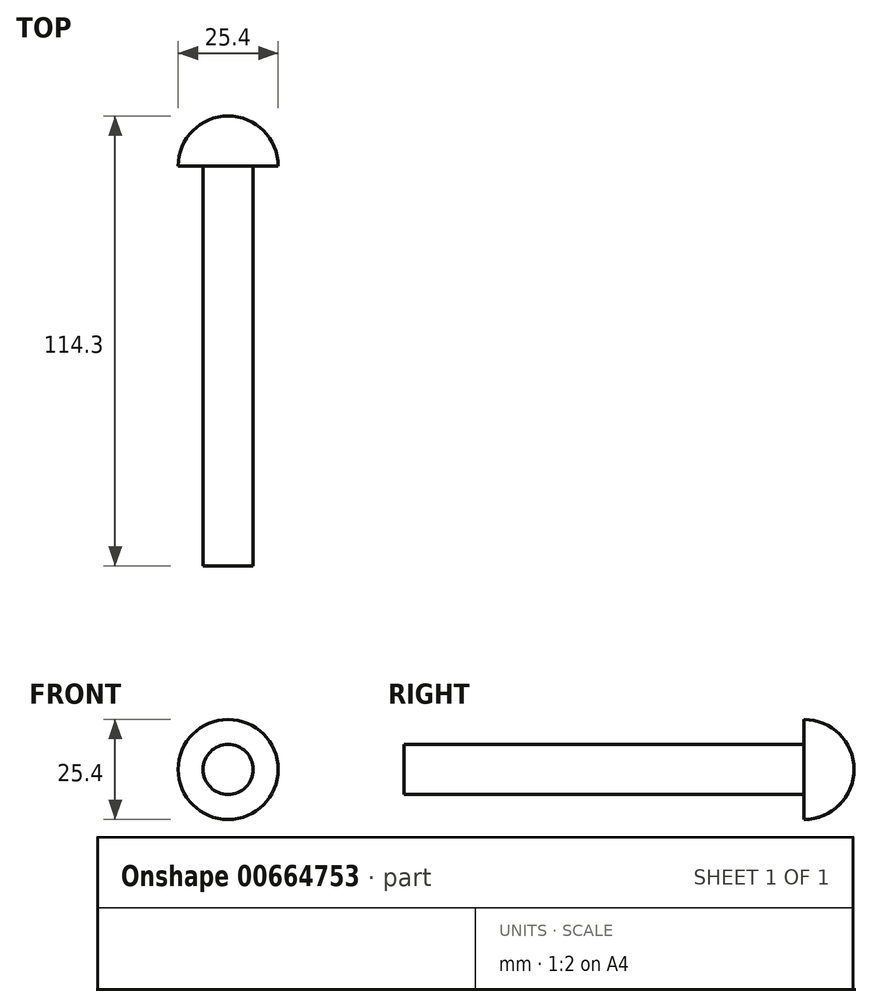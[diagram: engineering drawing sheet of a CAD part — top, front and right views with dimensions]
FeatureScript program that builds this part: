
annotation { "Feature Type Name" : "Feature", "Feature Type Description" : "" }
export const myFeature = defineFeature(function(context is Context, id is Id, definition is map)
    precondition{}
    {
        {
            var Q0;
            Q0=qCreatedBy(makeId("Front.planeOp"),FACE);
            var sketch = newSketch(context, id + "F0", { "sketchPlane" : qUnion([Q0])});
            skCircle(sketch, "E0", {"center": v(0, 0) * mm, "radius": 6.35 * mm});
            skSolve(sketch);
        }
        {
            var Q0;
            Q0 = qSketchRegion(id + "F0", true);
            extrude(context, id + "F1", {"entities" : qUnion([Q0]), "depth" : 101.6 * mm, "offsetDistance" : 25.4 * mm});
        }
        {
            var Q0;
            Q0=qCreatedBy(makeId("Right.planeOp"),FACE);
            var sketch = newSketch(context, id + "F2", { "sketchPlane" : qUnion([Q0])});
            skLineSegment(sketch, "E1", {"start": v(12.7, 0) * mm, "end": v(0, 0) * mm});
            skLineSegment(sketch, "E2", {"start": v(0, 0) * mm, "end": v(0, 12.7) * mm});
            skLineSegment(sketch, "E3", {"start": v(0, 12.7) * mm, "end": v(0, -12.43) * mm});
            skArc(sketch, "E4", {"start": v(0, 12.7) * mm, "mid": v(8.98, 8.98) * mm, "end": v(12.7, 0) * mm});
            skSolve(sketch);
        }
        {
            var Q0;
            Q0 = qSketchRegion(id + "F2", true);
            var Q1;
            Q1=sQuery(id+"F2.wireOp",EDGE,"E1");
            revolve(context, id + "F3", {"operationType" : NewBodyOperationType.ADD, "surfaceOperationType" : NewSurfaceOperationType.NEW, "entities" : qUnion([Q0]), "axis" : qUnion([Q1]), "revolveType" : RevolveType.FULL});
        }
    });
